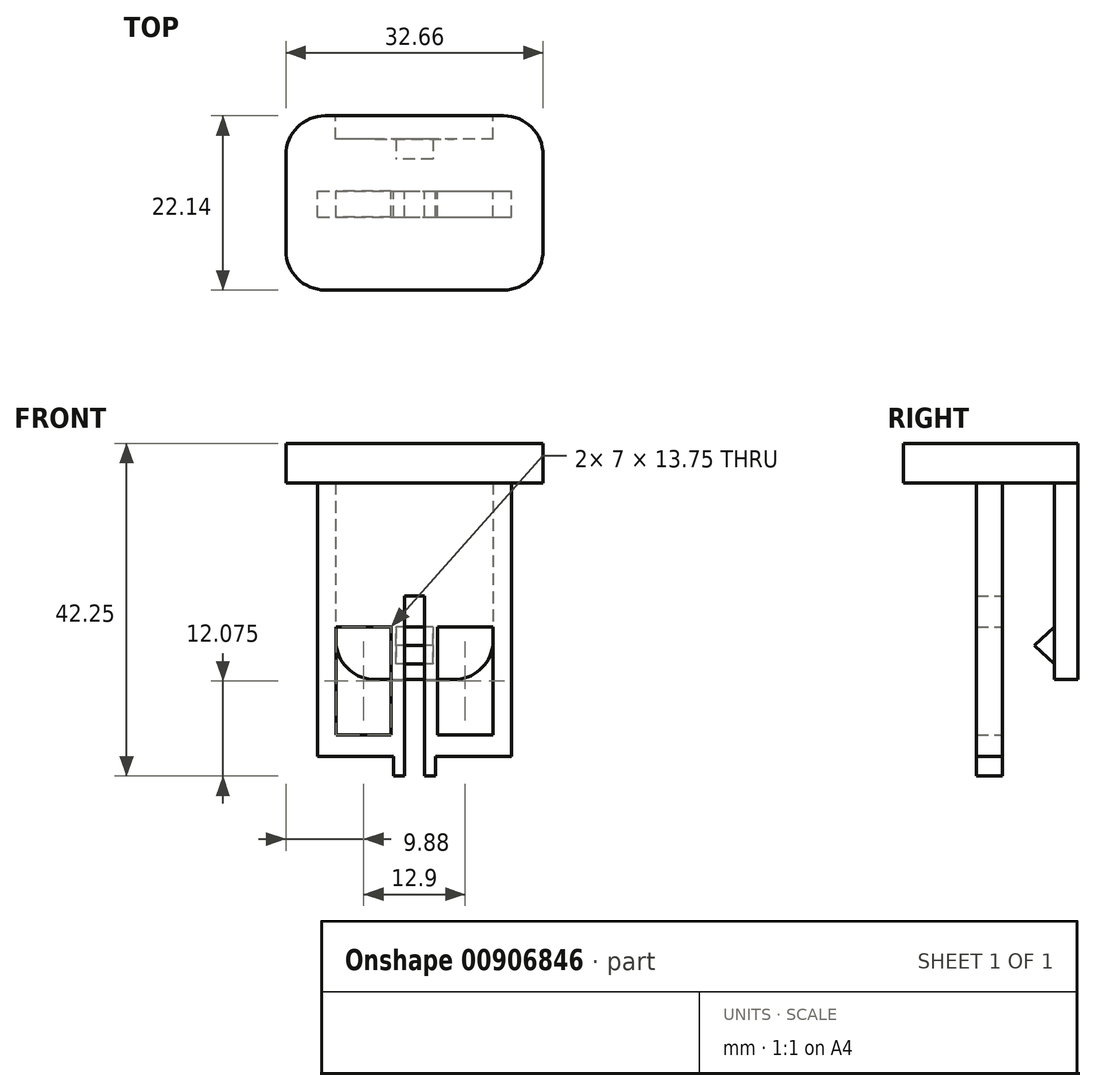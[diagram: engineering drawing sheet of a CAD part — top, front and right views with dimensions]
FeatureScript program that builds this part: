
annotation { "Feature Type Name" : "Feature", "Feature Type Description" : "" }
export const myFeature = defineFeature(function(context is Context, id is Id, definition is map)
    precondition{}
    {
        {
            var Q0;
            Q0=qCreatedBy(makeId("Top.planeOp"),FACE);
            var sketch = newSketch(context, id + "F0", { "sketchPlane" : qUnion([Q0])});
            skLineSegment(sketch, "E0.bottom", {"start": v(11.33, 11.07) * mm, "end": v(-11.33, 11.07) * mm});
            skLineSegment(sketch, "E0.top", {"start": v(11.33, -11.07) * mm, "end": v(-11.33, -11.07) * mm});
            skLineSegment(sketch, "E0.left", {"start": v(16.33, 6.07) * mm, "end": v(16.33, -6.07) * mm});
            skLineSegment(sketch, "E0.right", {"start": v(-16.33, 6.07) * mm, "end": v(-16.33, -6.07) * mm});
            skPoint(sketch, "E0.middle", {"position": v(0, 0) * mm});
            skPoint(sketch, "E1.visualSharp", {"position": v(-16.33, 11.07) * mm});
            skArc(sketch, "E1.filletArc", {"start": v(-11.33, 11.07) * mm, "mid": v(-14.87, 9.61) * mm, "end": v(-16.33, 6.07) * mm});
            skPoint(sketch, "E2.visualSharp", {"position": v(16.33, 11.07) * mm});
            skArc(sketch, "E2.filletArc", {"start": v(16.33, 6.07) * mm, "mid": v(14.87, 9.61) * mm, "end": v(11.33, 11.07) * mm});
            skPoint(sketch, "E3.visualSharp", {"position": v(16.33, -11.07) * mm});
            skArc(sketch, "E3.filletArc", {"start": v(11.33, -11.07) * mm, "mid": v(14.87, -9.61) * mm, "end": v(16.33, -6.07) * mm});
            skPoint(sketch, "E4.visualSharp", {"position": v(-16.33, -11.07) * mm});
            skArc(sketch, "E4.filletArc", {"start": v(-16.33, -6.08) * mm, "mid": v(-14.87, -9.61) * mm, "end": v(-11.33, -11.07) * mm});
            skSolve(sketch);
        }
        {
            var Q0;
            Q0 = qSketchRegion(id + "F0", true);
            extrude(context, id + "F1", {"entities" : qUnion([Q0]), "depth" : 5 * mm, "offsetDistance" : 25 * mm});
        }
        {
            var Q0;
            Q0=makeQuery(id+"F1.opExtrude","SWEPT_FACE",FACE,{"disambiguationData":[OSD([sQuery(id+"F0.wireOp",EDGE,"E0.bottom")])]});
            var sketch = newSketch(context, id + "F2", { "sketchPlane" : qUnion([Q0])});
            skLineSegment(sketch, "E5.bottom", {"start": v(10, 5) * mm, "end": v(-10, 5) * mm});
            skLineSegment(sketch, "E5.top", {"start": v(5, -25) * mm, "end": v(-5, -25) * mm});
            skLineSegment(sketch, "E5.left", {"start": v(10, 5) * mm, "end": v(10, -20) * mm});
            skLineSegment(sketch, "E5.right", {"start": v(-10, 5) * mm, "end": v(-10, -20) * mm});
            skPoint(sketch, "E6.visualSharp", {"position": v(10, -25) * mm});
            skArc(sketch, "E6.filletArc", {"start": v(5, -25) * mm, "mid": v(8.54, -23.54) * mm, "end": v(10, -20) * mm});
            skPoint(sketch, "E7.visualSharp", {"position": v(-10, -25) * mm});
            skArc(sketch, "E7.filletArc", {"start": v(-10, -20) * mm, "mid": v(-8.54, -23.54) * mm, "end": v(-5, -25) * mm});
            skSolve(sketch);
        }
        {
            var Q0;
            Q0 = qSketchRegion(id + "F2", true);
            extrude(context, id + "F3", {"entities" : qUnion([Q0]), "operationType" : NewBodyOperationType.ADD, "oppositeDirection" : true, "depth" : 3 * mm, "offsetDistance" : 25 * mm});
        }
        {
            var Q0;
            Q0=qCreatedBy(makeId("Right.planeOp"),FACE);
            var sketch = newSketch(context, id + "F4", { "sketchPlane" : qUnion([Q0])});
            skLineSegment(sketch, "E8", {"start": v(8.07, -23) * mm, "end": v(5.57, -20.64) * mm});
            skLineSegment(sketch, "E9", {"start": v(5.58, -20.64) * mm, "end": v(8.07, -18.29) * mm});
            skLineSegment(sketch, "E10", {"start": v(8.07, -18.29) * mm, "end": v(8.07, -23) * mm});
            skLineSegment(sketch, "E11", {"start": v(5.57, -20.64) * mm, "end": v(8.07, -20.64) * mm, "construction": true});
            skSolve(sketch);
        }
        {
            var Q0;
            Q0 = qSketchRegion(id + "F4", true);
            extrude(context, id + "F5", {"entities" : qUnion([Q0]), "operationType" : NewBodyOperationType.ADD, "depth" : 4.7 * mm, "offsetDistance" : 25 * mm, "symmetric" : true});
        }
        {
            var Q0;
            Q0=makeQuery(id+"F3.opExtrude","CAP_FACE",FACE,{"disambiguationData":[OSD([sQuery(id+"F2.wireOp",EDGE,"E5.bottom"),sQuery(id+"F2.wireOp",EDGE,"E5.top"),sQuery(id+"F2.wireOp",EDGE,"E5.left"),sQuery(id+"F2.wireOp",EDGE,"E5.right"),sQuery(id+"F2.wireOp",EDGE,"E6.filletArc"),sQuery(id+"F2.wireOp",EDGE,"E7.filletArc")])],"isStart":false});
            cPlane(context, id + "F6", {"entities" : qUnion([Q0]), "cplaneType" : CPlaneType.OFFSET, "offset" : 6.6 * mm, "width" : 150 * mm, "height" : 150 * mm});
        }
        {
            var Q0;
            Q0=qCreatedBy(id+"F6.planeOp",FACE);
            var sketch = newSketch(context, id + "F7", { "sketchPlane" : qUnion([Q0])});
            skLineSegment(sketch, "E12.bottom", {"start": v(-12.3, 5) * mm, "end": v(12.3, 5) * mm});
            skLineSegment(sketch, "E12.left", {"start": v(-12.3, 5) * mm, "end": v(-12.3, -34.75) * mm});
            skLineSegment(sketch, "E12.right", {"start": v(12.3, 5) * mm, "end": v(12.3, -34.75) * mm});
            skLineSegment(sketch, "E13", {"start": v(-12.3, -34.75) * mm, "end": v(-2.68, -34.75) * mm});
            skLineSegment(sketch, "E14", {"start": v(-2.68, -34.75) * mm, "end": v(-2.68, -37.25) * mm});
            skLineSegment(sketch, "E15", {"start": v(-2.68, -37.25) * mm, "end": v(-1.25, -37.25) * mm});
            skLineSegment(sketch, "E16", {"start": v(-1.25, -37.25) * mm, "end": v(-1.25, -14.34) * mm});
            skLineSegment(sketch, "E17", {"start": v(-1.25, -14.34) * mm, "end": v(1.25, -14.34) * mm});
            skLineSegment(sketch, "E18", {"start": v(1.25, -14.34) * mm, "end": v(1.25, -37.25) * mm});
            skLineSegment(sketch, "E19", {"start": v(1.25, -37.25) * mm, "end": v(2.68, -37.25) * mm});
            skLineSegment(sketch, "E20", {"start": v(2.68, -37.25) * mm, "end": v(2.68, -34.75) * mm});
            skLineSegment(sketch, "E21", {"start": v(2.68, -34.75) * mm, "end": v(12.3, -34.75) * mm});
            skLineSegment(sketch, "E22.bottom", {"start": v(2.95, -32.05) * mm, "end": v(9.95, -32.05) * mm});
            skLineSegment(sketch, "E22.top", {"start": v(2.95, -18.3) * mm, "end": v(9.95, -18.3) * mm});
            skLineSegment(sketch, "E22.left", {"start": v(2.95, -32.05) * mm, "end": v(2.95, -18.3) * mm});
            skLineSegment(sketch, "E22.right", {"start": v(9.95, -32.05) * mm, "end": v(9.95, -18.3) * mm});
            skLineSegment(sketch, "E23.bottom", {"start": v(-2.95, -32.05) * mm, "end": v(-9.95, -32.05) * mm});
            skLineSegment(sketch, "E23.top", {"start": v(-2.95, -18.3) * mm, "end": v(-9.95, -18.3) * mm});
            skLineSegment(sketch, "E23.left", {"start": v(-2.95, -32.05) * mm, "end": v(-2.95, -18.3) * mm});
            skLineSegment(sketch, "E23.right", {"start": v(-9.95, -32.05) * mm, "end": v(-9.95, -18.3) * mm});
            skSolve(sketch);
        }
        {
            var Q0;
            Q0 = qSketchRegion(id + "F7", true);
            extrude(context, id + "F8", {"entities" : qUnion([Q0]), "operationType" : NewBodyOperationType.ADD, "depth" : 3.3 * mm, "offsetDistance" : 25 * mm});
        }
    });
